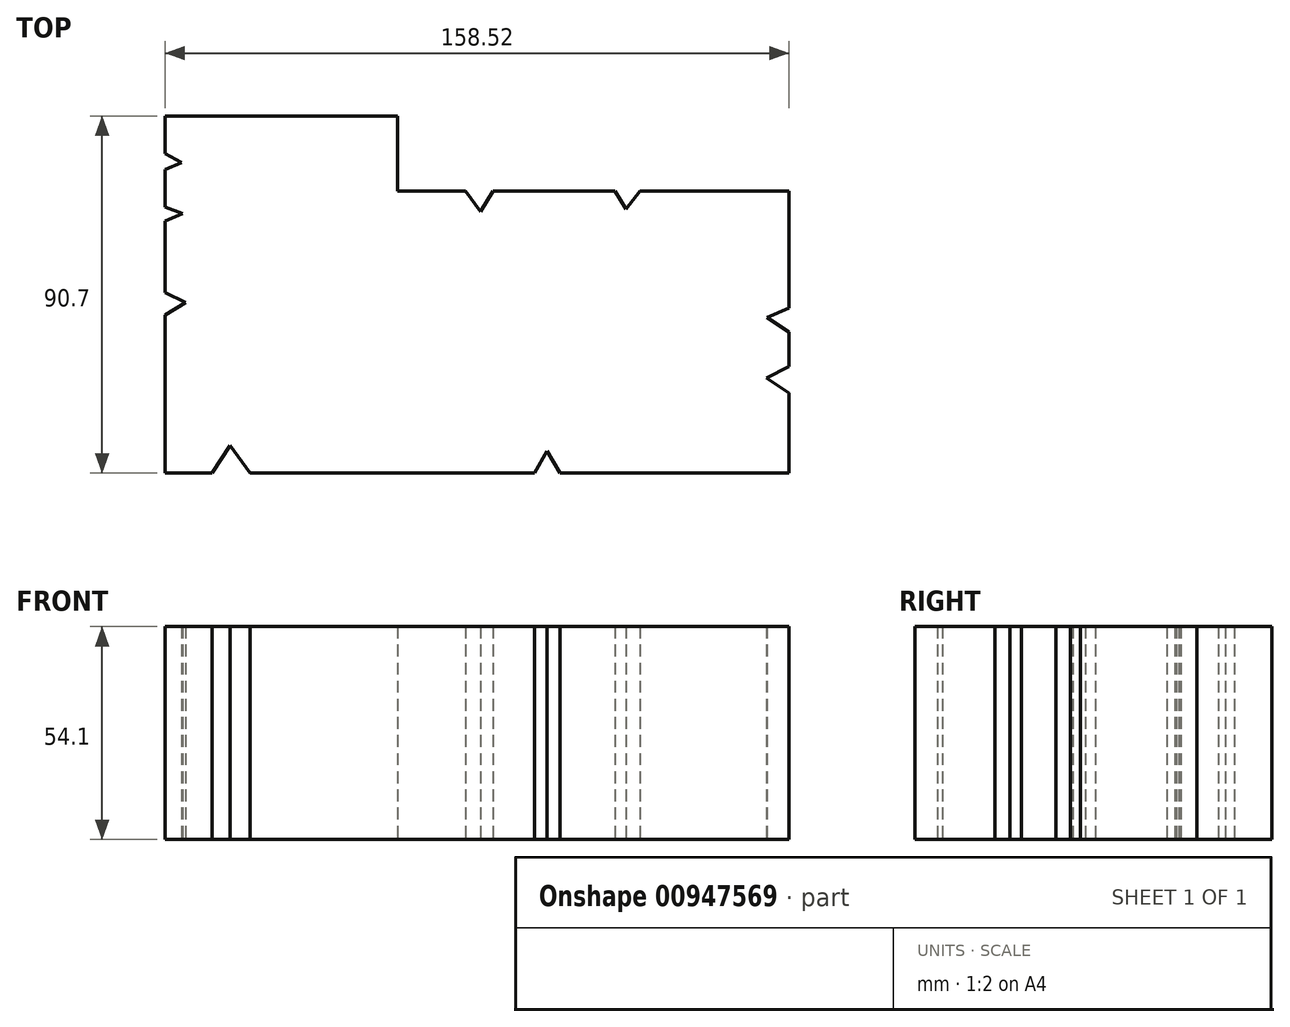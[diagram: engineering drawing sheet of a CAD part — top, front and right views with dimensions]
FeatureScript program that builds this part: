
annotation { "Feature Type Name" : "Feature", "Feature Type Description" : "" }
export const myFeature = defineFeature(function(context is Context, id is Id, definition is map)
    precondition{}
    {
        {
            var Q0;
            Q0=qCreatedBy(makeId("Top.planeOp"),FACE);
            var sketch = newSketch(context, id + "F0", { "sketchPlane" : qUnion([Q0])});
            skLineSegment(sketch, "E0.bottom", {"start": v(10.48, 44.57) * mm, "end": v(27.7, 44.57) * mm});
            skLineSegment(sketch, "E0.top", {"start": v(-48.65, -27) * mm, "end": v(-36.68, -27) * mm});
            skLineSegment(sketch, "E0.left", {"start": v(-48.65, 44.57) * mm, "end": v(-48.65, 40.51) * mm});
            skLineSegment(sketch, "E0.right", {"start": v(109.87, 44.57) * mm, "end": v(109.87, 14.97) * mm});
            skLineSegment(sketch, "E1.top", {"start": v(-48.65, 63.7) * mm, "end": v(10.48, 63.7) * mm});
            skLineSegment(sketch, "E1.left", {"start": v(-48.65, 44.57) * mm, "end": v(-48.65, 50.11) * mm});
            skLineSegment(sketch, "E1.right", {"start": v(10.48, 44.57) * mm, "end": v(10.48, 63.7) * mm});
            skLineSegment(sketch, "E2", {"start": v(-48.65, 54.13) * mm, "end": v(-44.43, 51.83) * mm});
            skLineSegment(sketch, "E3", {"start": v(-44.43, 51.83) * mm, "end": v(-48.65, 50.11) * mm});
            skLineSegment(sketch, "E4", {"start": v(-48.65, 40.51) * mm, "end": v(-44.22, 38.98) * mm});
            skLineSegment(sketch, "E5", {"start": v(-44.22, 38.98) * mm, "end": v(-48.65, 37) * mm});
            skLineSegment(sketch, "E6", {"start": v(-48.65, 18.8) * mm, "end": v(-43.44, 16.27) * mm});
            skLineSegment(sketch, "E7", {"start": v(-43.44, 16.27) * mm, "end": v(-48.65, 13.08) * mm});
            skLineSegment(sketch, "E8", {"start": v(109.87, 14.97) * mm, "end": v(104.3, 12.53) * mm});
            skLineSegment(sketch, "E9", {"start": v(104.3, 12.53) * mm, "end": v(109.87, 8.78) * mm});
            skLineSegment(sketch, "E10", {"start": v(109.87, 0) * mm, "end": v(104.13, -2.9) * mm});
            skLineSegment(sketch, "E11", {"start": v(104.13, -2.9) * mm, "end": v(109.87, -6.7) * mm});
            skLineSegment(sketch, "E12.trimOffspring", {"start": v(-48.65, 54.13) * mm, "end": v(-48.65, 63.7) * mm});
            skLineSegment(sketch, "E13.trimOffspring", {"start": v(-48.65, 37) * mm, "end": v(-48.65, 18.8) * mm});
            skLineSegment(sketch, "E14.trimOffspring", {"start": v(-48.65, 13.08) * mm, "end": v(-48.65, -27) * mm});
            skLineSegment(sketch, "E15.trimOffspring", {"start": v(109.87, 8.78) * mm, "end": v(109.87, 0) * mm});
            skLineSegment(sketch, "E16.trimOffspring", {"start": v(109.87, -6.7) * mm, "end": v(109.87, -27) * mm});
            skLineSegment(sketch, "E17", {"start": v(-36.68, -27) * mm, "end": v(-32.06, -19.97) * mm});
            skLineSegment(sketch, "E18", {"start": v(-32.06, -19.97) * mm, "end": v(-27.06, -27) * mm});
            skLineSegment(sketch, "E19", {"start": v(27.7, 44.57) * mm, "end": v(31.54, 39.4) * mm});
            skLineSegment(sketch, "E20", {"start": v(31.54, 39.4) * mm, "end": v(34.72, 44.57) * mm});
            skLineSegment(sketch, "E21", {"start": v(65.68, 44.57) * mm, "end": v(68.43, 40.01) * mm});
            skLineSegment(sketch, "E22", {"start": v(68.43, 40.01) * mm, "end": v(71.97, 44.57) * mm});
            skLineSegment(sketch, "E23.trimOffspring", {"start": v(71.97, 44.57) * mm, "end": v(109.87, 44.57) * mm});
            skLineSegment(sketch, "E24.trimOffspring", {"start": v(34.72, 44.57) * mm, "end": v(65.68, 44.57) * mm});
            skLineSegment(sketch, "E25.trimOffspring", {"start": v(-27.06, -27) * mm, "end": v(45.23, -27) * mm});
            skLineSegment(sketch, "E26", {"start": v(45.23, -27) * mm, "end": v(48.46, -21.35) * mm});
            skLineSegment(sketch, "E27", {"start": v(48.46, -21.35) * mm, "end": v(51.75, -27) * mm});
            skLineSegment(sketch, "E28.trimOffspring", {"start": v(51.75, -27) * mm, "end": v(109.87, -27) * mm});
            skSolve(sketch);
        }
        {
            var Q0;
            Q0=makeQuery(id+"F0.imprint","IMPRINT",FACE,{"disambiguationData":[TD([[makeQuery(id+"F0.imprint","IMPRINT",EDGE,{"derivedFrom":sQuery(id+"F0.wireOp",EDGE,"E0.bottom")}),-1.0]])]});
            extrude(context, id + "F1", {"entities" : qUnion([Q0]), "depth" : 54.1 * mm, "offsetDistance" : 25.4 * mm});
        }
    });
